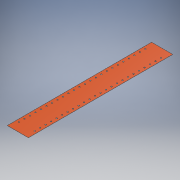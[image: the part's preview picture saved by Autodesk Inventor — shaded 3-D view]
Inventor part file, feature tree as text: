
AUTODESK INVENTOR PART (.ipt)
format: ipt  version: 2019 (Build 230136000, 136)  size: 206,336 bytes
history: native  units: mm
features: extrude x2, other x2, mirror x1
ambient origin geometry x8: Origin, YZ Plane, XZ Plane, XY Plane, X Axis, Y Axis, Z Axis, Center Point
bodies: Body1 (feature_tree)
feature tree (5):
  extrude  "Skin Body"  Depth=1256.0mm
  extrude  "End Cut"  Depth=628.0mm
  mirror  "End Cut Mirror"
  other  "Skin Scheme"
  other  "End Cut Outline"
